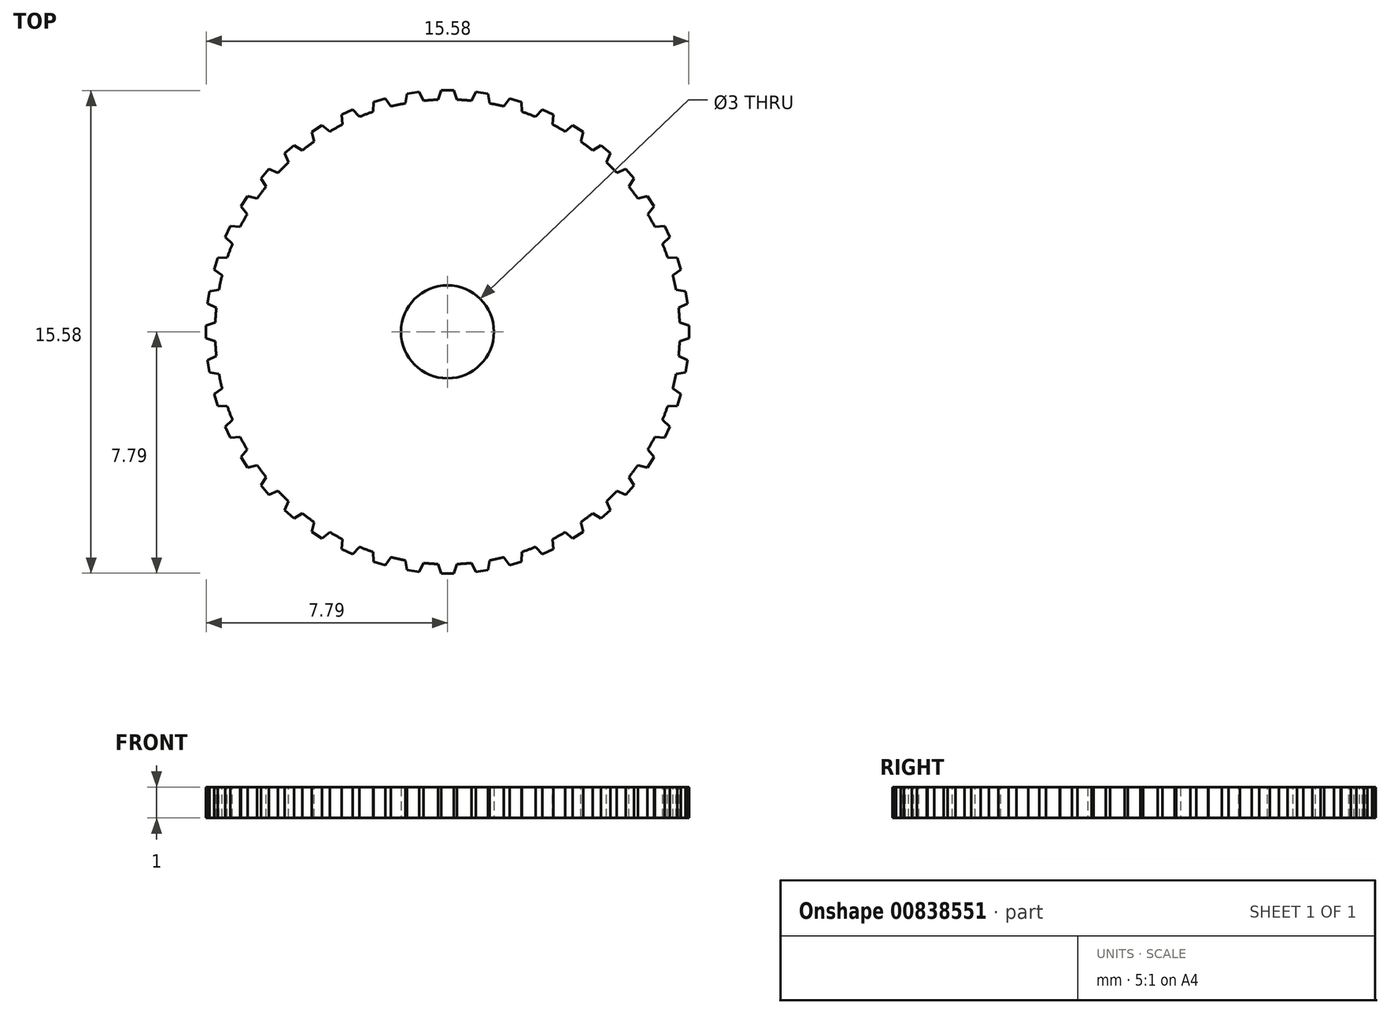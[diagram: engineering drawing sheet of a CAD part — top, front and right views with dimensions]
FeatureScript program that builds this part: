
annotation { "Feature Type Name" : "Feature", "Feature Type Description" : "" }
export const myFeature = defineFeature(function(context is Context, id is Id, definition is map)
    precondition{}
    {
        {
            assignVariable(context, id + "F0", {"name" : "ID", "anyValue" : 15});
        }
        {
            assignVariable(context, id + "F1", {"name" : "IW", "anyValue" : 0.6});
        }
        {
            assignVariable(context, id + "F2", {"name" : "GD", "anyValue" : 1});
        }
        {
            var Q0;
            Q0=qCreatedBy(makeId("Top.planeOp"),FACE);
            var sketch = newSketch(context, id + "F3", { "sketchPlane" : qUnion([Q0])});
            skCircle(sketch, "E0", {"center": v(0, 0) * mm, "radius": 7.5 * mm});
            skSolve(sketch);
        }
        {
            var Q0;
            Q0 = qSketchRegion(id + "F3", true);
            extrude(context, id + "F4", {"entities" : qUnion([Q0]), "depth" : (getVariable(context, 'GD')) * mm, "offsetDistance" : 25 * mm});
        }
        {
            var Q0;
            Q0=makeQuery(id+"F4.opExtrude","CAP_FACE",FACE,{"disambiguationData":[OSD([sQuery(id+"F3.wireOp",EDGE,"E0")])],"isStart":false});
            var sketch = newSketch(context, id + "F5", { "sketchPlane" : qUnion([Q0])});
            skLineSegment(sketch, "E1", {"start": v(0, 0) * mm, "end": v(14.18, 0) * mm, "construction": true});
            skLineSegment(sketch, "E2", {"start": v(7.8, 0.2) * mm, "end": v(7.8, -0.2) * mm});
            skLineSegment(sketch, "E3", {"start": v(7.8, -0.2) * mm, "end": v(7.5, -0.3) * mm});
            skLineSegment(sketch, "E4", {"start": v(7.5, -0.3) * mm, "end": v(7.5, 0.3) * mm, "construction": true});
            skLineSegment(sketch, "E5", {"start": v(7.5, 0.3) * mm, "end": v(7.8, 0.2) * mm});
            skLineSegment(sketch, "E6", {"start": v(7.5, 0.3) * mm, "end": v(7.4, 0.3) * mm});
            skLineSegment(sketch, "E7", {"start": v(7.4, 0.3) * mm, "end": v(7.4, -0.3) * mm});
            skLineSegment(sketch, "E8", {"start": v(7.4, -0.3) * mm, "end": v(7.5, -0.3) * mm});
            skSolve(sketch);
        }
        {
            assignVariable(context, id + "F6", {"name" : "TM1", "anyValue" : 3.14 * 2 * getVariable(context, 'ID')});
        }
        {
            assignVariable(context, id + "F7", {"name" : "NoT", "anyValue" : floor((getVariable(context, 'TM1')) / (3.5 * getVariable(context, 'IW')))});
        }
        {
            var Q0;
            Q0 = qSketchRegion(id + "F5", true);
            extrude(context, id + "F8", {"entities" : qUnion([Q0]), "oppositeDirection" : true, "depth" : (getVariable(context, 'GD')) * mm, "offsetDistance" : 25 * mm});
        }
        {
            var Q0;
            Q0=makeQuery(id+"F8.opExtrude","SWEPT_BODY",BODY,{"disambiguationData":[OSD([sQuery(id+"F5.wireOp",EDGE,"E2"),sQuery(id+"F5.wireOp",EDGE,"E3"),sQuery(id+"F5.wireOp",EDGE,"E5"),sQuery(id+"F5.wireOp",EDGE,"E6"),sQuery(id+"F5.wireOp",EDGE,"E7"),sQuery(id+"F5.wireOp",EDGE,"E8")])]});
            var Q1;
            Q1=makeQuery(id+"F4.opExtrude","SWEPT_FACE",FACE,{"disambiguationData":[OSD([sQuery(id+"F3.wireOp",EDGE,"E0")])]});
            circularPattern(context, id + "F9", {"operationType" : NewBodyOperationType.ADD, "entities" : qUnion([Q0]), "axis" : qUnion([Q1]), "angle" : 360 * degree, "instanceCount" : getVariable(context, 'NoT'), "equalSpace" : true});
        }
        {
            var Q0;
            {var subQ0=makeQuery(id+"F8.opExtrude","CAP_FACE",FACE,{"disambiguationData":[OSD([sQuery(id+"F5.wireOp",EDGE,"E2"),sQuery(id+"F5.wireOp",EDGE,"E3"),sQuery(id+"F5.wireOp",EDGE,"E5"),sQuery(id+"F5.wireOp",EDGE,"E6"),sQuery(id+"F5.wireOp",EDGE,"E7"),sQuery(id+"F5.wireOp",EDGE,"E8")])],"isStart":false});Q0=makeQuery(id+"F9.boolean.opBoolean","MERGE",FACE,{"derivedFrom":[makeQuery(id+"F4.opExtrude","CAP_FACE",FACE,{"disambiguationData":[OSD([sQuery(id+"F3.wireOp",EDGE,"E0")])],"isStart":true}),subQ0,makeQuery(id+"F9.opPattern","COPY",FACE,{"derivedFrom":subQ0,"instanceName":"1"}),makeQuery(id+"F9.opPattern","COPY",FACE,{"derivedFrom":subQ0,"instanceName":"2"}),makeQuery(id+"F9.opPattern","COPY",FACE,{"derivedFrom":subQ0,"instanceName":"3"}),makeQuery(id+"F9.opPattern","COPY",FACE,{"derivedFrom":subQ0,"instanceName":"4"}),makeQuery(id+"F9.opPattern","COPY",FACE,{"derivedFrom":subQ0,"instanceName":"5"}),makeQuery(id+"F9.opPattern","COPY",FACE,{"derivedFrom":subQ0,"instanceName":"6"}),makeQuery(id+"F9.opPattern","COPY",FACE,{"derivedFrom":subQ0,"instanceName":"7"}),makeQuery(id+"F9.opPattern","COPY",FACE,{"derivedFrom":subQ0,"instanceName":"8"}),makeQuery(id+"F9.opPattern","COPY",FACE,{"derivedFrom":subQ0,"instanceName":"9"}),makeQuery(id+"F9.opPattern","COPY",FACE,{"derivedFrom":subQ0,"instanceName":"10"}),makeQuery(id+"F9.opPattern","COPY",FACE,{"derivedFrom":subQ0,"instanceName":"11"}),makeQuery(id+"F9.opPattern","COPY",FACE,{"derivedFrom":subQ0,"instanceName":"12"}),makeQuery(id+"F9.opPattern","COPY",FACE,{"derivedFrom":subQ0,"instanceName":"13"}),makeQuery(id+"F9.opPattern","COPY",FACE,{"derivedFrom":subQ0,"instanceName":"14"}),makeQuery(id+"F9.opPattern","COPY",FACE,{"derivedFrom":subQ0,"instanceName":"15"}),makeQuery(id+"F9.opPattern","COPY",FACE,{"derivedFrom":subQ0,"instanceName":"16"}),makeQuery(id+"F9.opPattern","COPY",FACE,{"derivedFrom":subQ0,"instanceName":"17"}),makeQuery(id+"F9.opPattern","COPY",FACE,{"derivedFrom":subQ0,"instanceName":"18"}),makeQuery(id+"F9.opPattern","COPY",FACE,{"derivedFrom":subQ0,"instanceName":"19"}),makeQuery(id+"F9.opPattern","COPY",FACE,{"derivedFrom":subQ0,"instanceName":"20"}),makeQuery(id+"F9.opPattern","COPY",FACE,{"derivedFrom":subQ0,"instanceName":"21"}),makeQuery(id+"F9.opPattern","COPY",FACE,{"derivedFrom":subQ0,"instanceName":"22"}),makeQuery(id+"F9.opPattern","COPY",FACE,{"derivedFrom":subQ0,"instanceName":"23"}),makeQuery(id+"F9.opPattern","COPY",FACE,{"derivedFrom":subQ0,"instanceName":"24"}),makeQuery(id+"F9.opPattern","COPY",FACE,{"derivedFrom":subQ0,"instanceName":"25"}),makeQuery(id+"F9.opPattern","COPY",FACE,{"derivedFrom":subQ0,"instanceName":"26"}),makeQuery(id+"F9.opPattern","COPY",FACE,{"derivedFrom":subQ0,"instanceName":"27"}),makeQuery(id+"F9.opPattern","COPY",FACE,{"derivedFrom":subQ0,"instanceName":"28"}),makeQuery(id+"F9.opPattern","COPY",FACE,{"derivedFrom":subQ0,"instanceName":"29"}),makeQuery(id+"F9.opPattern","COPY",FACE,{"derivedFrom":subQ0,"instanceName":"30"}),makeQuery(id+"F9.opPattern","COPY",FACE,{"derivedFrom":subQ0,"instanceName":"31"}),makeQuery(id+"F9.opPattern","COPY",FACE,{"derivedFrom":subQ0,"instanceName":"32"}),makeQuery(id+"F9.opPattern","COPY",FACE,{"derivedFrom":subQ0,"instanceName":"33"}),makeQuery(id+"F9.opPattern","COPY",FACE,{"derivedFrom":subQ0,"instanceName":"34"}),makeQuery(id+"F9.opPattern","COPY",FACE,{"derivedFrom":subQ0,"instanceName":"35"}),makeQuery(id+"F9.opPattern","COPY",FACE,{"derivedFrom":subQ0,"instanceName":"36"}),makeQuery(id+"F9.opPattern","COPY",FACE,{"derivedFrom":subQ0,"instanceName":"37"}),makeQuery(id+"F9.opPattern","COPY",FACE,{"derivedFrom":subQ0,"instanceName":"38"}),makeQuery(id+"F9.opPattern","COPY",FACE,{"derivedFrom":subQ0,"instanceName":"39"}),makeQuery(id+"F9.opPattern","COPY",FACE,{"derivedFrom":subQ0,"instanceName":"40"}),makeQuery(id+"F9.opPattern","COPY",FACE,{"derivedFrom":subQ0,"instanceName":"41"}),makeQuery(id+"F9.opPattern","COPY",FACE,{"derivedFrom":subQ0,"instanceName":"42"}),makeQuery(id+"F9.opPattern","COPY",FACE,{"derivedFrom":subQ0,"instanceName":"43"})]});}
            var sketch = newSketch(context, id + "F10", { "sketchPlane" : qUnion([Q0])});
            skCircle(sketch, "E9", {"center": v(0, 0) * mm, "radius": 1.5 * mm});
            skSolve(sketch);
        }
        {
            var Q0;
            Q0=makeQuery(id+"F10.imprint","IMPRINT",FACE,{"disambiguationData":[TD([[makeQuery(id+"F10.imprint","IMPRINT",EDGE,{"derivedFrom":sQuery(id+"F10.wireOp",EDGE,"E9")}),1.0]])]});
            var Q1;
            {var subQ0=makeQuery(id+"F8.opExtrude","CAP_FACE",FACE,{"disambiguationData":[OSD([sQuery(id+"F5.wireOp",EDGE,"E2"),sQuery(id+"F5.wireOp",EDGE,"E3"),sQuery(id+"F5.wireOp",EDGE,"E5"),sQuery(id+"F5.wireOp",EDGE,"E6"),sQuery(id+"F5.wireOp",EDGE,"E7"),sQuery(id+"F5.wireOp",EDGE,"E8")])],"isStart":true});Q1=makeQuery(id+"F9.boolean.opBoolean","MERGE",FACE,{"derivedFrom":[makeQuery(id+"F4.opExtrude","CAP_FACE",FACE,{"disambiguationData":[OSD([sQuery(id+"F3.wireOp",EDGE,"E0")])],"isStart":false}),subQ0,makeQuery(id+"F9.opPattern","COPY",FACE,{"derivedFrom":subQ0,"instanceName":"1"}),makeQuery(id+"F9.opPattern","COPY",FACE,{"derivedFrom":subQ0,"instanceName":"2"}),makeQuery(id+"F9.opPattern","COPY",FACE,{"derivedFrom":subQ0,"instanceName":"3"}),makeQuery(id+"F9.opPattern","COPY",FACE,{"derivedFrom":subQ0,"instanceName":"4"}),makeQuery(id+"F9.opPattern","COPY",FACE,{"derivedFrom":subQ0,"instanceName":"5"}),makeQuery(id+"F9.opPattern","COPY",FACE,{"derivedFrom":subQ0,"instanceName":"6"}),makeQuery(id+"F9.opPattern","COPY",FACE,{"derivedFrom":subQ0,"instanceName":"7"}),makeQuery(id+"F9.opPattern","COPY",FACE,{"derivedFrom":subQ0,"instanceName":"8"}),makeQuery(id+"F9.opPattern","COPY",FACE,{"derivedFrom":subQ0,"instanceName":"9"}),makeQuery(id+"F9.opPattern","COPY",FACE,{"derivedFrom":subQ0,"instanceName":"10"}),makeQuery(id+"F9.opPattern","COPY",FACE,{"derivedFrom":subQ0,"instanceName":"11"}),makeQuery(id+"F9.opPattern","COPY",FACE,{"derivedFrom":subQ0,"instanceName":"12"}),makeQuery(id+"F9.opPattern","COPY",FACE,{"derivedFrom":subQ0,"instanceName":"13"}),makeQuery(id+"F9.opPattern","COPY",FACE,{"derivedFrom":subQ0,"instanceName":"14"}),makeQuery(id+"F9.opPattern","COPY",FACE,{"derivedFrom":subQ0,"instanceName":"15"}),makeQuery(id+"F9.opPattern","COPY",FACE,{"derivedFrom":subQ0,"instanceName":"16"}),makeQuery(id+"F9.opPattern","COPY",FACE,{"derivedFrom":subQ0,"instanceName":"17"}),makeQuery(id+"F9.opPattern","COPY",FACE,{"derivedFrom":subQ0,"instanceName":"18"}),makeQuery(id+"F9.opPattern","COPY",FACE,{"derivedFrom":subQ0,"instanceName":"19"}),makeQuery(id+"F9.opPattern","COPY",FACE,{"derivedFrom":subQ0,"instanceName":"20"}),makeQuery(id+"F9.opPattern","COPY",FACE,{"derivedFrom":subQ0,"instanceName":"21"}),makeQuery(id+"F9.opPattern","COPY",FACE,{"derivedFrom":subQ0,"instanceName":"22"}),makeQuery(id+"F9.opPattern","COPY",FACE,{"derivedFrom":subQ0,"instanceName":"23"}),makeQuery(id+"F9.opPattern","COPY",FACE,{"derivedFrom":subQ0,"instanceName":"24"}),makeQuery(id+"F9.opPattern","COPY",FACE,{"derivedFrom":subQ0,"instanceName":"25"}),makeQuery(id+"F9.opPattern","COPY",FACE,{"derivedFrom":subQ0,"instanceName":"26"}),makeQuery(id+"F9.opPattern","COPY",FACE,{"derivedFrom":subQ0,"instanceName":"27"}),makeQuery(id+"F9.opPattern","COPY",FACE,{"derivedFrom":subQ0,"instanceName":"28"}),makeQuery(id+"F9.opPattern","COPY",FACE,{"derivedFrom":subQ0,"instanceName":"29"}),makeQuery(id+"F9.opPattern","COPY",FACE,{"derivedFrom":subQ0,"instanceName":"30"}),makeQuery(id+"F9.opPattern","COPY",FACE,{"derivedFrom":subQ0,"instanceName":"31"}),makeQuery(id+"F9.opPattern","COPY",FACE,{"derivedFrom":subQ0,"instanceName":"32"}),makeQuery(id+"F9.opPattern","COPY",FACE,{"derivedFrom":subQ0,"instanceName":"33"}),makeQuery(id+"F9.opPattern","COPY",FACE,{"derivedFrom":subQ0,"instanceName":"34"}),makeQuery(id+"F9.opPattern","COPY",FACE,{"derivedFrom":subQ0,"instanceName":"35"}),makeQuery(id+"F9.opPattern","COPY",FACE,{"derivedFrom":subQ0,"instanceName":"36"}),makeQuery(id+"F9.opPattern","COPY",FACE,{"derivedFrom":subQ0,"instanceName":"37"}),makeQuery(id+"F9.opPattern","COPY",FACE,{"derivedFrom":subQ0,"instanceName":"38"}),makeQuery(id+"F9.opPattern","COPY",FACE,{"derivedFrom":subQ0,"instanceName":"39"}),makeQuery(id+"F9.opPattern","COPY",FACE,{"derivedFrom":subQ0,"instanceName":"40"}),makeQuery(id+"F9.opPattern","COPY",FACE,{"derivedFrom":subQ0,"instanceName":"41"}),makeQuery(id+"F9.opPattern","COPY",FACE,{"derivedFrom":subQ0,"instanceName":"42"}),makeQuery(id+"F9.opPattern","COPY",FACE,{"derivedFrom":subQ0,"instanceName":"43"})]});}
            extrude(context, id + "F11", {"entities" : qUnion([Q0]), "operationType" : NewBodyOperationType.REMOVE, "endBound" : BoundingType.UP_TO_SURFACE, "oppositeDirection" : true, "depth" : 25 * mm, "endBoundEntityFace" : qUnion([Q1]), "offsetDistance" : 25 * mm});
        }
    });
